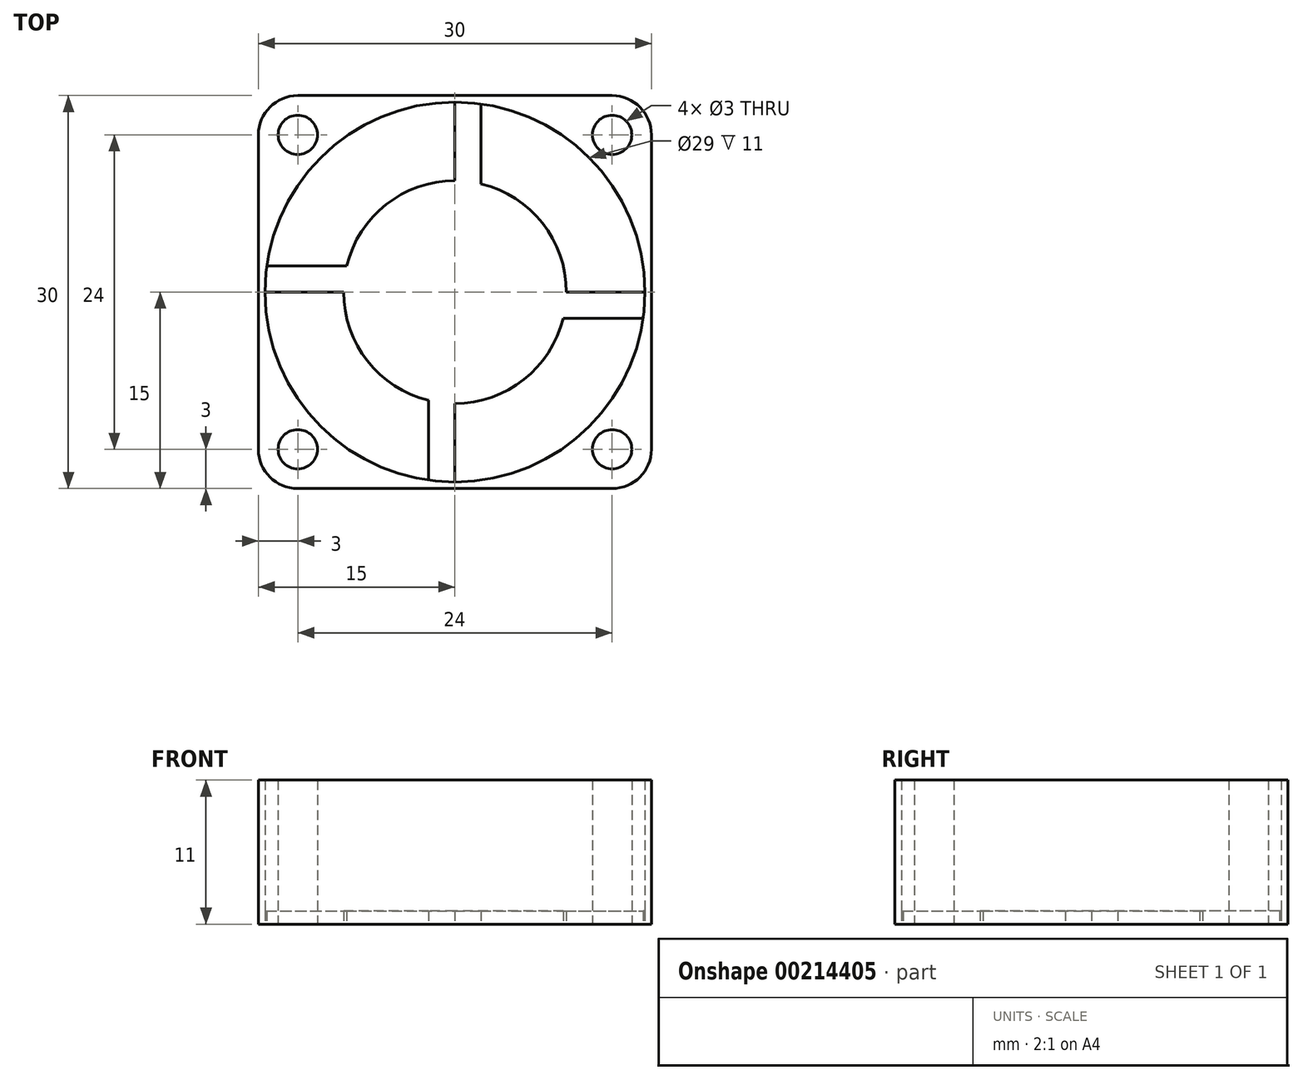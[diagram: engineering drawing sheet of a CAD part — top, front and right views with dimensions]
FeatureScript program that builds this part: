
annotation { "Feature Type Name" : "Feature", "Feature Type Description" : "" }
export const myFeature = defineFeature(function(context is Context, id is Id, definition is map)
    precondition{}
    {
        {
            var Q0;
            Q0=qCreatedBy(makeId("Top.planeOp"),FACE);
            var sketch = newSketch(context, id + "F0", { "sketchPlane" : qUnion([Q0])});
            skLineSegment(sketch, "E0.bottom", {"start": v(12, -15) * mm, "end": v(-12, -15) * mm});
            skLineSegment(sketch, "E0.top", {"start": v(12, 15) * mm, "end": v(-12, 15) * mm});
            skLineSegment(sketch, "E0.left", {"start": v(15, -12) * mm, "end": v(15, 12) * mm});
            skLineSegment(sketch, "E0.right", {"start": v(-15, -12) * mm, "end": v(-15, 12) * mm});
            skPoint(sketch, "E0.middle", {"position": v(0, 0) * mm});
            skCircle(sketch, "E1", {"center": v(0, 0) * mm, "radius": 14.5 * mm});
            skCircle(sketch, "E2", {"center": v(-12, 12) * mm, "radius": 1.5 * mm});
            skPoint(sketch, "E3.visualSharp", {"position": v(-15, 15) * mm});
            skArc(sketch, "E3.filletArc", {"start": v(-12, 15) * mm, "mid": v(-14.12, 14.12) * mm, "end": v(-15, 12) * mm});
            skPoint(sketch, "E4.visualSharp", {"position": v(15, 15) * mm});
            skArc(sketch, "E4.filletArc", {"start": v(15, 12) * mm, "mid": v(14.12, 14.12) * mm, "end": v(12, 15) * mm});
            skPoint(sketch, "E5.visualSharp", {"position": v(15, -15) * mm});
            skArc(sketch, "E5.filletArc", {"start": v(12, -15) * mm, "mid": v(14.12, -14.12) * mm, "end": v(15, -12) * mm});
            skPoint(sketch, "E6.visualSharp", {"position": v(-15, -15) * mm});
            skArc(sketch, "E6.filletArc", {"start": v(-15, -12) * mm, "mid": v(-14.12, -14.12) * mm, "end": v(-12, -15) * mm});
            skCircle(sketch, "E7", {"center": v(12, 12) * mm, "radius": 1.5 * mm});
            skCircle(sketch, "E8", {"center": v(12, -12) * mm, "radius": 1.5 * mm});
            skCircle(sketch, "E9", {"center": v(-12, -12) * mm, "radius": 1.5 * mm});
            skSolve(sketch);
        }
        {
            var Q0;
            Q0 = qSketchRegion(id + "F0", true);
            extrude(context, id + "F1", {"entities" : qUnion([Q0]), "depth" : 11 * mm});
        }
        {
            var Q0;
            Q0=makeQuery(id+"F1.opExtrude","CAP_FACE",FACE,{"disambiguationData":[OSD([sQuery(id+"F0.wireOp",EDGE,"E0.bottom"),sQuery(id+"F0.wireOp",EDGE,"E0.top"),sQuery(id+"F0.wireOp",EDGE,"E0.left"),sQuery(id+"F0.wireOp",EDGE,"E0.right"),sQuery(id+"F0.wireOp",EDGE,"E1"),sQuery(id+"F0.wireOp",EDGE,"E2"),sQuery(id+"F0.wireOp",EDGE,"E3.filletArc"),sQuery(id+"F0.wireOp",EDGE,"E4.filletArc"),sQuery(id+"F0.wireOp",EDGE,"E5.filletArc"),sQuery(id+"F0.wireOp",EDGE,"E6.filletArc"),sQuery(id+"F0.wireOp",EDGE,"E7"),sQuery(id+"F0.wireOp",EDGE,"E8"),sQuery(id+"F0.wireOp",EDGE,"E9")])],"isStart":true});
            var sketch = newSketch(context, id + "F2", { "sketchPlane" : qUnion([Q0])});
            skArc(sketch, "E10", {"start": v(2, -8.26) * mm, "mid": v(6.68, -5.26) * mm, "end": v(8.5, 0) * mm});
            skLineSegment(sketch, "E11", {"start": v(8.5, 0) * mm, "end": v(15, 0) * mm});
            skLineSegment(sketch, "E12", {"start": v(0, 15) * mm, "end": v(0, 8.5) * mm});
            skLineSegment(sketch, "E13", {"start": v(-15, 0) * mm, "end": v(-8.5, 0) * mm});
            skLineSegment(sketch, "E14", {"start": v(0, -15) * mm, "end": v(0, -8.5) * mm});
            skLineSegment(sketch, "E15.0", {"start": v(2, -15) * mm, "end": v(2, -8.26) * mm});
            skLineSegment(sketch, "E16.0", {"start": v(8.26, 2) * mm, "end": v(15, 2) * mm});
            skLineSegment(sketch, "E17.0", {"start": v(-2, 15) * mm, "end": v(-2, 8.26) * mm});
            skLineSegment(sketch, "E18.0", {"start": v(-15, -2) * mm, "end": v(-8.26, -2) * mm});
            skLineSegment(sketch, "E19", {"start": v(-15, 0) * mm, "end": v(-15, -2) * mm});
            skLineSegment(sketch, "E20", {"start": v(0, -15) * mm, "end": v(2, -15) * mm});
            skLineSegment(sketch, "E21", {"start": v(15, 0) * mm, "end": v(15, 2) * mm});
            skLineSegment(sketch, "E22", {"start": v(0, 15) * mm, "end": v(-2, 15) * mm});
            skLineSegment(sketch, "E23.trimOffspring", {"start": v(0, -2) * mm, "end": v(0, 0) * mm});
            skArc(sketch, "E24.trimOffspring", {"start": v(8.26, 2) * mm, "mid": v(5.26, 6.68) * mm, "end": v(0, 8.5) * mm});
            skArc(sketch, "E25.trimOffspring", {"start": v(-2, 8.26) * mm, "mid": v(-6.68, 5.26) * mm, "end": v(-8.5, 0) * mm});
            skArc(sketch, "E26.trimOffspring", {"start": v(-8.26, -2) * mm, "mid": v(-5.26, -6.68) * mm, "end": v(0, -8.5) * mm});
            skSolve(sketch);
        }
        {
            var Q0;
            Q0 = qSketchRegion(id + "F2", true);
            extrude(context, id + "F3", {"entities" : qUnion([Q0]), "operationType" : NewBodyOperationType.ADD, "oppositeDirection" : true, "depth" : 1 * mm});
        }
    });
